# Revit family: Toilet_Seat-Elongated_Closed_Front-KOHLER-C3-230-K-4108BR_1
name_source: partatom
category: Plumbing Fixtures
revit_build: Autodesk Revit 2017 (Build: 20160225_1515(x64)
units: mm (PartAtom-declared; Revit-internal decimal feet)

## family parameters
Cut with Voids When Loaded = No
Host = Face
OmniClass Number = 23.31.19.19.17
OmniClass Title = Water Closet Seats
Part Type = Normal
Room Calculation Point = No
Round Connector Dimension = Use Diameter
Shared = No

## types (1)
- 0-White
    ADA Compliant = No
    Apparent Load = 2400 VA
    Assembly Code = D2010100
    CW Connection = Yes
    Cold Water Inlet = Cold Water Inlet
    Date Modified = 01/14/2021
    Default Elevation = 0"
    Description = Electronic toilet seat with bidet function - 110V
    Electrical Connector = Yes
    Electrical Note = Route the electrical and install to a 220-240V GFCI- or ELCB-protected Receptacle
    Finish = Kohler-Plastic-0-White
    Flow Rate = 0 GPM
    HW Connection = No
    Height = 6 3/16"
    Hot Water Inlet = Hot Water Inlet
    Length = 20 7/16"
    Manufacturer = KOHLER Co.
    Master Format 2014 = 22 41 13.13
    Master Format 2014 Name = Residential Water Closets
    Material = Plastic
    Model = K-4108BR-0
    Pressure = 0.00 psi
    Product Documentation Link = http://resources.kohler.com
    Product Name = C3-230
    Product Page URL = https://www.br.kohler.com
    Type = 1
    URL = https://br.kohler.com
    Vent Connection = No
    Voltage = 240 V
    Waste Connection = No
    Waste Water Outlet = Waste Water Outlet
    WaterSense Certified = No
    Width = 17 1/8"

## geometry (parser evidence)
native form markers: Sweep x7
no freeform markers — native parametric forms only
